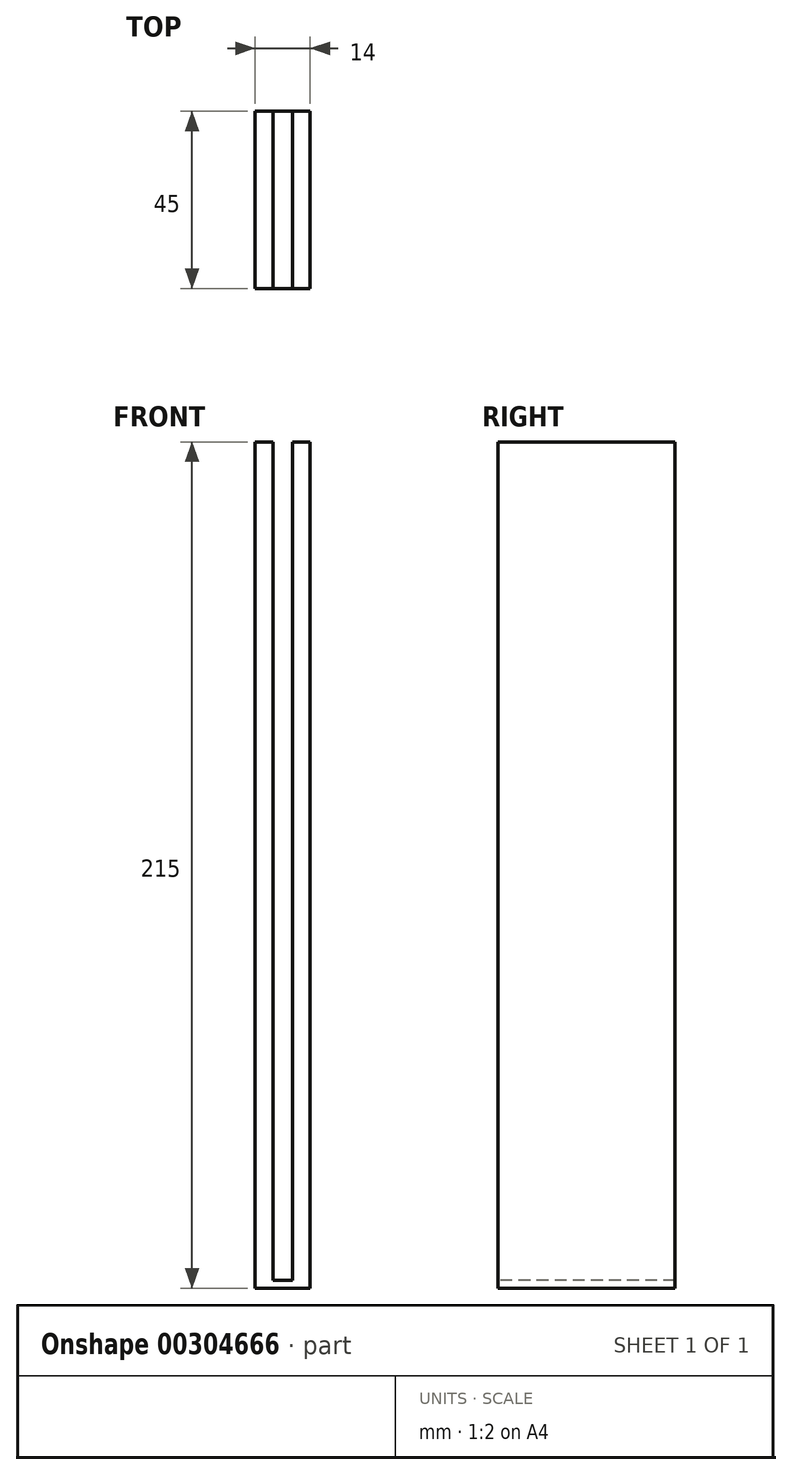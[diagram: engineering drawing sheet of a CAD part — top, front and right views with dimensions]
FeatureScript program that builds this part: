
annotation { "Feature Type Name" : "Feature", "Feature Type Description" : "" }
export const myFeature = defineFeature(function(context is Context, id is Id, definition is map)
    precondition{}
    {
        {
            var Q0;
            Q0=qCreatedBy(makeId("Right.planeOp"),FACE);
            var sketch = newSketch(context, id + "F0", { "sketchPlane" : qUnion([Q0])});
            skLineSegment(sketch, "E0.bottom", {"start": v(-13.7, -30.18) * mm, "end": v(31.3, -30.18) * mm});
            skLineSegment(sketch, "E0.top", {"start": v(-13.7, 184.82) * mm, "end": v(31.3, 184.82) * mm});
            skLineSegment(sketch, "E0.left", {"start": v(-13.7, -30.18) * mm, "end": v(-13.7, 184.82) * mm});
            skLineSegment(sketch, "E0.right", {"start": v(31.3, -30.18) * mm, "end": v(31.3, 184.82) * mm});
            skSolve(sketch);
        }
        {
            var Q0;
            Q0 = qSketchRegion(id + "F0", true);
            extrude(context, id + "F1", {"entities" : qUnion([Q0]), "depth" : 7 * mm, "hasSecondDirection" : true, "secondDirectionOppositeDirection" : true, "secondDirectionDepth" : 7 * mm});
        }
        {
            var Q0;
            Q0=makeQuery(id+"F1.opExtrude","SWEPT_FACE",FACE,{"disambiguationData":[OSD([sQuery(id+"F0.wireOp",EDGE,"E0.left")])]});
            var sketch = newSketch(context, id + "F2", { "sketchPlane" : qUnion([Q0])});
            skLineSegment(sketch, "E1", {"start": v(0, 184.82) * mm, "end": v(0, 184.82) * mm});
            skPoint(sketch, "E1.endSnap0", {"position": v(0, 184.82) * mm});
            skLineSegment(sketch, "E2", {"start": v(0, 184.82) * mm, "end": v(2.5, 184.82) * mm, "construction": true});
            skLineSegment(sketch, "E3", {"start": v(0, 184.82) * mm, "end": v(-2.5, 184.82) * mm, "construction": true});
            skPoint(sketch, "E4.endSnap0", {"position": v(0, -30.18) * mm});
            skLineSegment(sketch, "E5.bottom", {"start": v(-2.5, 184.82) * mm, "end": v(2.5, 184.82) * mm});
            skLineSegment(sketch, "E5.top", {"start": v(-2.5, -28.18) * mm, "end": v(2.5, -28.18) * mm});
            skLineSegment(sketch, "E5.left", {"start": v(-2.5, 184.82) * mm, "end": v(-2.5, -28.18) * mm});
            skLineSegment(sketch, "E5.right", {"start": v(2.5, 184.82) * mm, "end": v(2.5, -28.18) * mm});
            skSolve(sketch);
        }
        {
            var Q0;
            Q0 = qSketchRegion(id + "F2", true);
            extrude(context, id + "F3", {"entities" : qUnion([Q0]), "operationType" : NewBodyOperationType.REMOVE, "oppositeDirection" : true, "depth" : 70 * mm, "hasSecondDirection" : true, "secondDirectionOppositeDirection" : false, "secondDirectionDepth" : 25 * mm});
        }
    });
